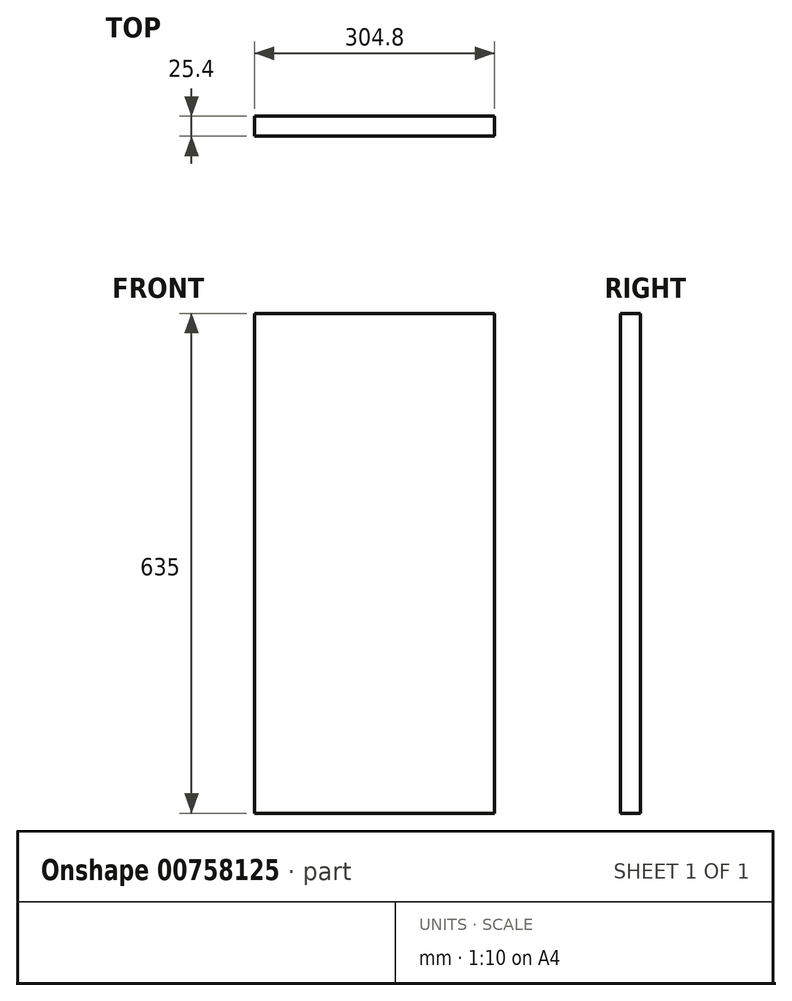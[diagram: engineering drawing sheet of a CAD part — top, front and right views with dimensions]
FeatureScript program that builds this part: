
annotation { "Feature Type Name" : "Feature", "Feature Type Description" : "" }
export const myFeature = defineFeature(function(context is Context, id is Id, definition is map)
    precondition{}
    {
        {
            var Q0;
            Q0=qCreatedBy(makeId("Top.planeOp"),FACE);
            var sketch = newSketch(context, id + "F0", { "sketchPlane" : qUnion([Q0])});
            skLineSegment(sketch, "E0.bottom", {"start": v(-106.7, 46.37) * mm, "end": v(198.1, 46.37) * mm});
            skLineSegment(sketch, "E0.top", {"start": v(-106.7, 20.97) * mm, "end": v(198.1, 20.97) * mm});
            skLineSegment(sketch, "E0.left", {"start": v(-106.7, 46.37) * mm, "end": v(-106.7, 20.97) * mm});
            skLineSegment(sketch, "E0.right", {"start": v(198.1, 46.37) * mm, "end": v(198.1, 20.97) * mm});
            skSolve(sketch);
        }
        {
            var Q0;
            Q0 = qSketchRegion(id + "F0", true);
            extrude(context, id + "F1", {"entities" : qUnion([Q0]), "depth" : 635 * mm, "offsetDistance" : 25.4 * mm});
        }
    });
